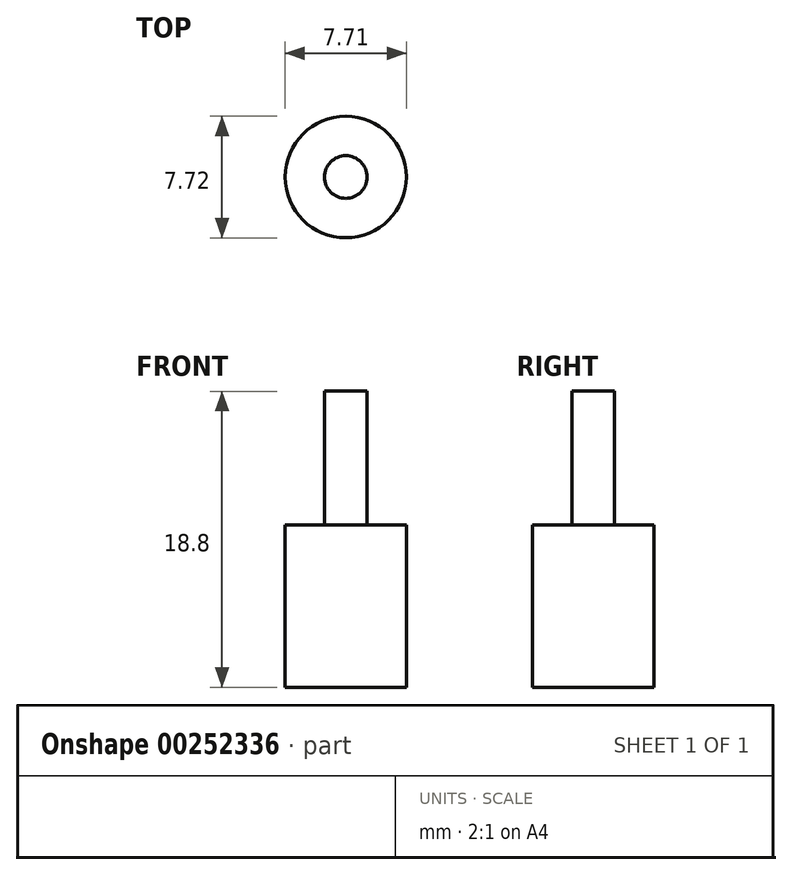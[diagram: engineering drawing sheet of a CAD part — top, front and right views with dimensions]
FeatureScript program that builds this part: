
annotation { "Feature Type Name" : "Feature", "Feature Type Description" : "" }
export const myFeature = defineFeature(function(context is Context, id is Id, definition is map)
    precondition{}
    {
        {
            var Q0;
            Q0=qCreatedBy(makeId("Front.planeOp"),FACE);
            var sketch = newSketch(context, id + "F0", { "sketchPlane" : qUnion([Q0])});
            skLineSegment(sketch, "E0.bottom", {"start": v(-1.93, 5.15) * mm, "end": v(1.93, 5.15) * mm});
            skLineSegment(sketch, "E0.top", {"start": v(-1.93, -5.15) * mm, "end": v(1.93, -5.15) * mm});
            skLineSegment(sketch, "E0.left", {"start": v(-1.93, 5.15) * mm, "end": v(-1.93, -5.15) * mm});
            skLineSegment(sketch, "E0.right", {"start": v(1.93, 5.15) * mm, "end": v(1.93, -5.15) * mm});
            skPoint(sketch, "E0.middle", {"position": v(0, 0) * mm});
            skSolve(sketch);
        }
        {
            var Q0;
            Q0=qSketchRegion(id+"F0",true);
            var Q1;
            Q1=sQuery(id+"F0.wireOp",EDGE,"E0.right");
            revolve(context, id + "F1", {"entities" : qUnion([Q0]), "axis" : qUnion([Q1]), "revolveType" : RevolveType.FULL});
        }
        {
            var Q0;
            Q0=makeQuery(id+"F1.opRevolve","SWEPT_FACE",FACE,{"disambiguationData":[OSD([sQuery(id+"F0.wireOp",EDGE,"E0.bottom")])]});
            shell(context, id + "F2", {"entities" : qUnion([Q0]), "thickness" : 2.5 * mm});
        }
        {
            var Q0;
            Q0=makeQuery(id+"F2.opShell","OFFSET_FACE",FACE,{"disambiguationData":[OSD([sQuery(id+"F0.wireOp",EDGE,"E0.top")])]});
            extrude(context, id + "F3", {"entities" : qUnion([Q0]), "operationType" : NewBodyOperationType.ADD, "depth" : 16.3 * mm});
        }
    });
